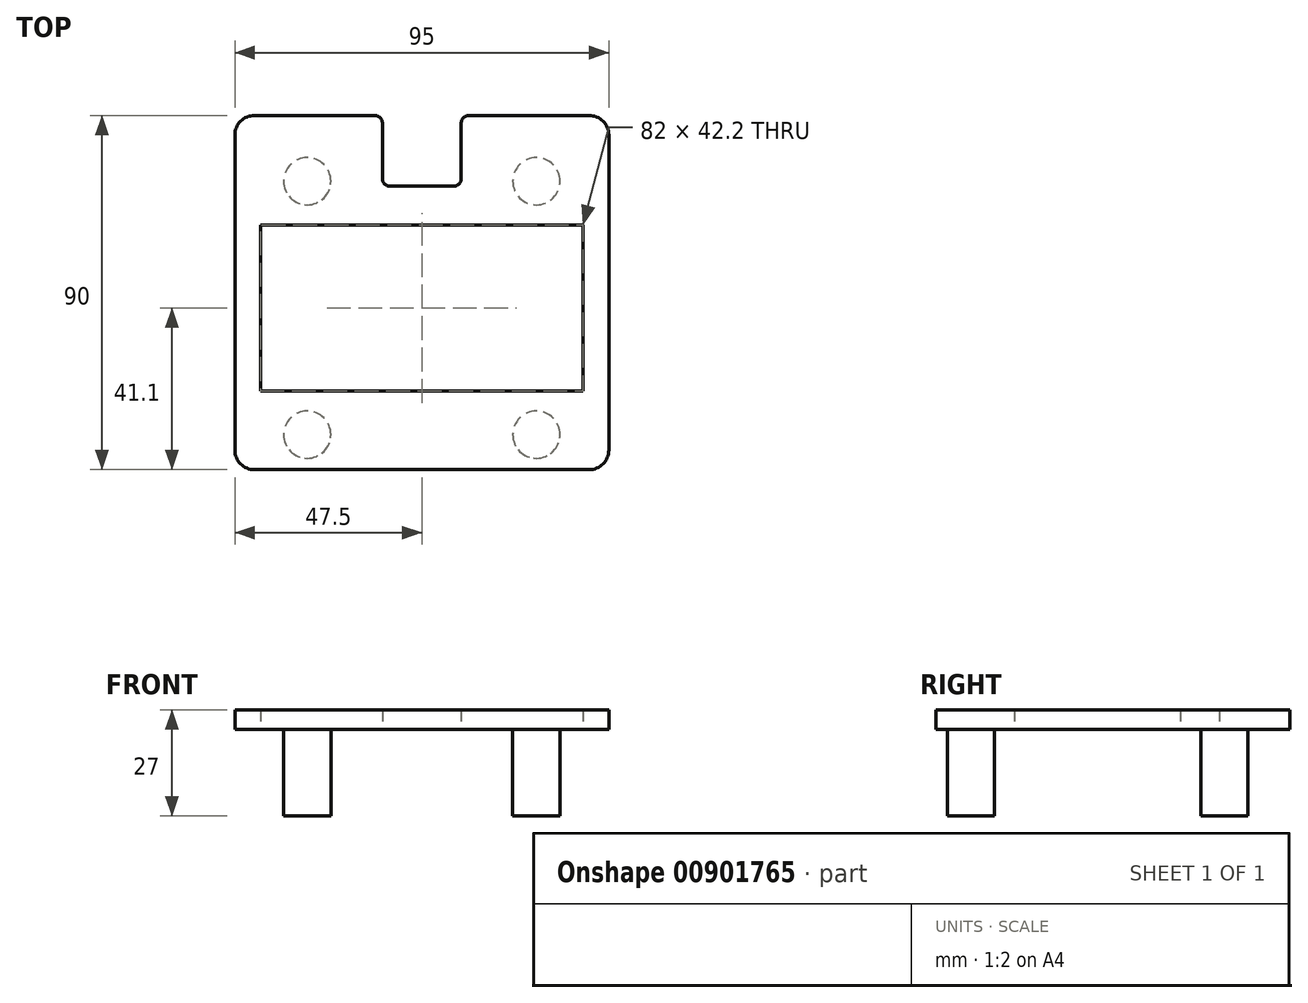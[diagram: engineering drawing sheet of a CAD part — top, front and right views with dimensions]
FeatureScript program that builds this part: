
annotation { "Feature Type Name" : "Feature", "Feature Type Description" : "" }
export const myFeature = defineFeature(function(context is Context, id is Id, definition is map)
    precondition{}
    {
        {
            var Q0;
            Q0=qCreatedBy(makeId("Top.planeOp"),FACE);
            var sketch = newSketch(context, id + "F0", { "sketchPlane" : qUnion([Q0])});
            skLineSegment(sketch, "E0.bottom", {"start": v(0, 0) * mm, "end": v(82, 0) * mm});
            skLineSegment(sketch, "E0.top", {"start": v(0, 42.2) * mm, "end": v(82, 42.2) * mm});
            skLineSegment(sketch, "E0.left", {"start": v(0, 0) * mm, "end": v(0, 42.2) * mm});
            skLineSegment(sketch, "E0.right", {"start": v(82, 0) * mm, "end": v(82, 42.2) * mm});
            skLineSegment(sketch, "E1.bottom", {"start": v(-1.5, -20) * mm, "end": v(83.5, -20) * mm});
            skLineSegment(sketch, "E1.top", {"start": v(-1.5, 70) * mm, "end": v(29, 70) * mm});
            skLineSegment(sketch, "E1.left", {"start": v(-6.5, -15) * mm, "end": v(-6.5, 65) * mm});
            skLineSegment(sketch, "E1.right", {"start": v(88.5, -15) * mm, "end": v(88.5, 65) * mm});
            skLineSegment(sketch, "E2", {"start": v(49, 52) * mm, "end": v(33, 52) * mm});
            skLineSegment(sketch, "E3", {"start": v(31, 54) * mm, "end": v(31, 68) * mm});
            skLineSegment(sketch, "E4", {"start": v(51, 54) * mm, "end": v(51, 68) * mm});
            skLineSegment(sketch, "E5.trimOffspring", {"start": v(53, 70) * mm, "end": v(83.5, 70) * mm});
            skPoint(sketch, "E6.visualSharp", {"position": v(-6.5, 70) * mm});
            skArc(sketch, "E6.filletArc", {"start": v(-1.5, 70) * mm, "mid": v(-5.04, 68.54) * mm, "end": v(-6.5, 65) * mm});
            skPoint(sketch, "E7.visualSharp", {"position": v(31, 70) * mm});
            skArc(sketch, "E7.filletArc", {"start": v(31, 68) * mm, "mid": v(30.41, 69.41) * mm, "end": v(29, 70) * mm});
            skPoint(sketch, "E8.visualSharp", {"position": v(31, 52) * mm});
            skArc(sketch, "E8.filletArc", {"start": v(31, 54) * mm, "mid": v(31.59, 52.59) * mm, "end": v(33, 52) * mm});
            skPoint(sketch, "E9.visualSharp", {"position": v(51, 52) * mm});
            skArc(sketch, "E9.filletArc", {"start": v(49, 52) * mm, "mid": v(50.41, 52.59) * mm, "end": v(51, 54) * mm});
            skPoint(sketch, "E10.visualSharp", {"position": v(51, 70) * mm});
            skArc(sketch, "E10.filletArc", {"start": v(53, 70) * mm, "mid": v(51.59, 69.41) * mm, "end": v(51, 68) * mm});
            skPoint(sketch, "E11.visualSharp", {"position": v(88.5, 70) * mm});
            skArc(sketch, "E11.filletArc", {"start": v(88.5, 65) * mm, "mid": v(87.04, 68.54) * mm, "end": v(83.5, 70) * mm});
            skPoint(sketch, "E12.visualSharp", {"position": v(88.5, -20) * mm});
            skArc(sketch, "E12.filletArc", {"start": v(83.5, -20) * mm, "mid": v(87.04, -18.54) * mm, "end": v(88.5, -15) * mm});
            skPoint(sketch, "E13.visualSharp", {"position": v(-6.5, -20) * mm});
            skArc(sketch, "E13.filletArc", {"start": v(-6.5, -15) * mm, "mid": v(-5.04, -18.54) * mm, "end": v(-1.5, -20) * mm});
            skSolve(sketch);
        }
        {
            var Q0;
            Q0 = qSketchRegion(id + "F0", true);
            extrude(context, id + "F1", {"entities" : qUnion([Q0]), "depth" : 5 * mm, "offsetDistance" : 25 * mm});
        }
        {
            var Q0;
            Q0=makeQuery(id+"F1.opExtrude","CAP_FACE",FACE,{"disambiguationData":[OSD([sQuery(id+"F0.wireOp",EDGE,"E0.bottom"),sQuery(id+"F0.wireOp",EDGE,"E0.top"),sQuery(id+"F0.wireOp",EDGE,"E0.left"),sQuery(id+"F0.wireOp",EDGE,"E0.right"),sQuery(id+"F0.wireOp",EDGE,"E1.bottom"),sQuery(id+"F0.wireOp",EDGE,"E1.top"),sQuery(id+"F0.wireOp",EDGE,"E1.left"),sQuery(id+"F0.wireOp",EDGE,"E1.right"),sQuery(id+"F0.wireOp",EDGE,"E2"),sQuery(id+"F0.wireOp",EDGE,"E3"),sQuery(id+"F0.wireOp",EDGE,"E4"),sQuery(id+"F0.wireOp",EDGE,"E5.trimOffspring"),sQuery(id+"F0.wireOp",EDGE,"E6.filletArc"),sQuery(id+"F0.wireOp",EDGE,"E7.filletArc"),sQuery(id+"F0.wireOp",EDGE,"E8.filletArc"),sQuery(id+"F0.wireOp",EDGE,"E9.filletArc"),sQuery(id+"F0.wireOp",EDGE,"E10.filletArc"),sQuery(id+"F0.wireOp",EDGE,"E11.filletArc"),sQuery(id+"F0.wireOp",EDGE,"E12.filletArc"),sQuery(id+"F0.wireOp",EDGE,"E13.filletArc")])],"isStart":true});
            var sketch = newSketch(context, id + "F2", { "sketchPlane" : qUnion([Q0])});
            skCircle(sketch, "E14", {"center": v(70.1, -53.3) * mm, "radius": 6 * mm});
            skLineSegment(sketch, "E15", {"start": v(41, -52) * mm, "end": v(41, 20) * mm, "construction": true});
            skLineSegment(sketch, "E16", {"start": v(82, -21.1) * mm, "end": v(0, -21.1) * mm, "construction": true});
            skCircle(sketch, "E17.MirrorC", {"center": v(11.9, -53.3) * mm, "radius": 6 * mm});
            skLineSegment(sketch, "E18.MirrorCS", {"start": v(0, -21.1) * mm, "end": v(82, -21.1) * mm, "construction": true});
            skCircle(sketch, "E19.MirrorC", {"center": v(70.1, 11.1) * mm, "radius": 6 * mm});
            skCircle(sketch, "E20.MirrorC", {"center": v(11.9, 11.1) * mm, "radius": 6 * mm});
            skLineSegment(sketch, "E21", {"start": v(81.2, -64.2) * mm, "end": v(0, -64.2) * mm, "construction": true});
            skSolve(sketch);
        }
        {
            var Q0;
            Q0 = qSketchRegion(id + "F2", true);
            extrude(context, id + "F3", {"entities" : qUnion([Q0]), "operationType" : NewBodyOperationType.ADD, "depth" : 22 * mm, "offsetDistance" : 25 * mm});
        }
    });
